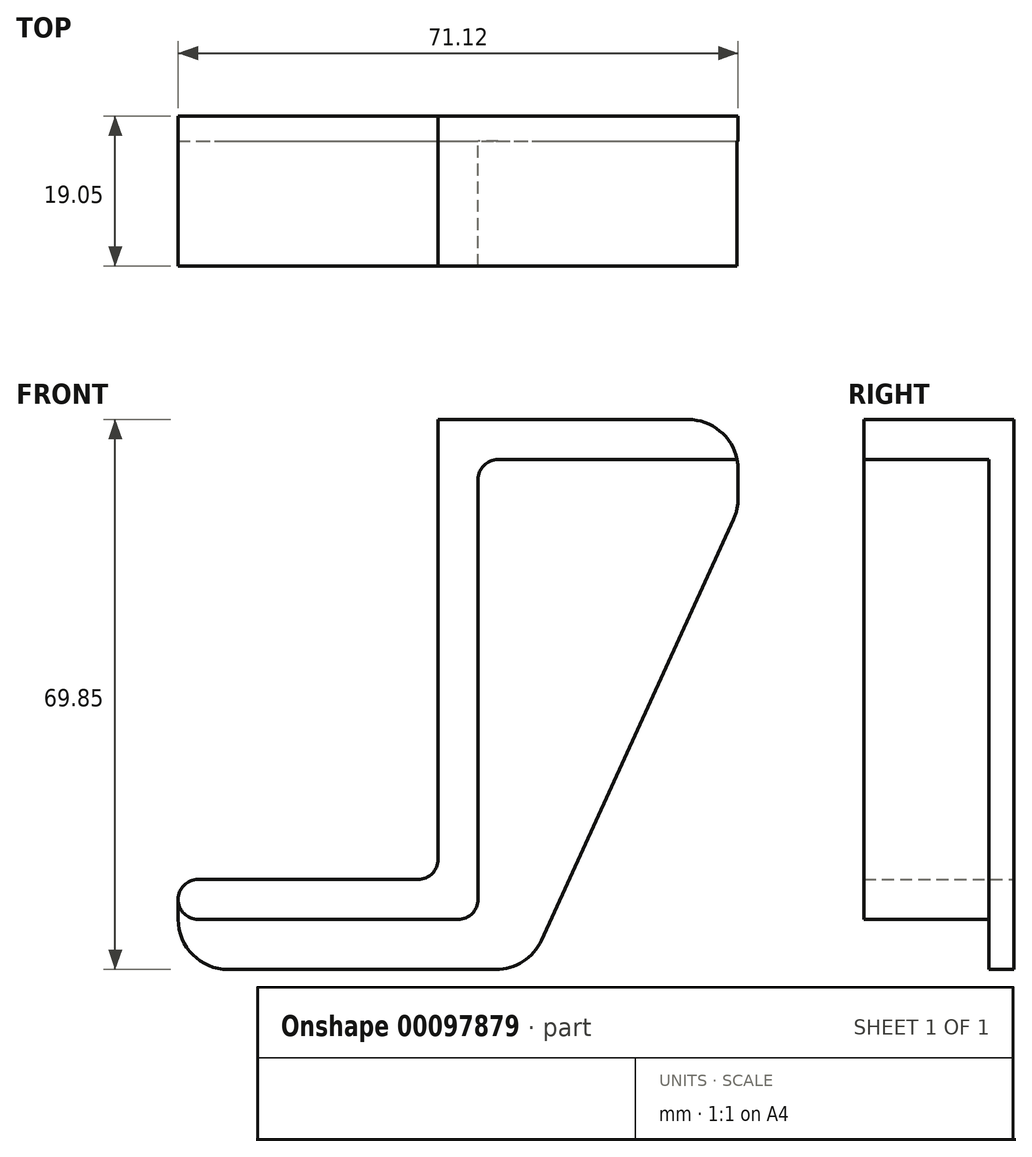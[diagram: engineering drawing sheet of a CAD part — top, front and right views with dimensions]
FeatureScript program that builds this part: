
annotation { "Feature Type Name" : "Feature", "Feature Type Description" : "" }
export const myFeature = defineFeature(function(context is Context, id is Id, definition is map)
    precondition{}
    {
        {
            var Q0;
            Q0=qCreatedBy(makeId("Front.planeOp"),FACE);
            var sketch = newSketch(context, id + "F0", { "sketchPlane" : qUnion([Q0])});
            skLineSegment(sketch, "E0.bottom", {"start": v(0, 0) * mm, "end": v(5.08, 0) * mm});
            skLineSegment(sketch, "E0.top", {"start": v(0, 63.5) * mm, "end": v(5.08, 63.5) * mm});
            skLineSegment(sketch, "E0.left", {"start": v(0, 5.08) * mm, "end": v(0, 63.5) * mm});
            skLineSegment(sketch, "E0.right", {"start": v(5.08, 0) * mm, "end": v(5.08, 58.42) * mm});
            skLineSegment(sketch, "E1.bottom", {"start": v(5.08, 0) * mm, "end": v(-33.02, 0) * mm});
            skLineSegment(sketch, "E1.top", {"start": v(0, 5.08) * mm, "end": v(-33.02, 5.08) * mm});
            skLineSegment(sketch, "E1.left", {"start": v(5.08, 0) * mm, "end": v(5.08, 5.08) * mm});
            skLineSegment(sketch, "E1.right", {"start": v(-33.02, 0) * mm, "end": v(-33.02, 5.08) * mm});
            skLineSegment(sketch, "E2.bottom", {"start": v(0, 63.5) * mm, "end": v(38.1, 63.5) * mm});
            skLineSegment(sketch, "E2.top", {"start": v(5.08, 58.42) * mm, "end": v(38.1, 58.42) * mm});
            skLineSegment(sketch, "E2.left", {"start": v(0, 63.5) * mm, "end": v(0, 58.42) * mm});
            skLineSegment(sketch, "E2.right", {"start": v(38.1, 63.5) * mm, "end": v(38.1, 58.42) * mm});
            skLineSegment(sketch, "E3.bottom", {"start": v(-33.02, 0) * mm, "end": v(5.08, 0) * mm});
            skLineSegment(sketch, "E3.top", {"start": v(-26.67, -6.35) * mm, "end": v(7.35, -6.35) * mm});
            skLineSegment(sketch, "E3.left", {"start": v(-33.02, 0) * mm, "end": v(-33.02, 0) * mm});
            skPoint(sketch, "E4.visualSharp", {"position": v(-33.02, -6.35) * mm});
            skArc(sketch, "E4.filletArc", {"start": v(-33.02, 0) * mm, "mid": v(-31.16, -4.5) * mm, "end": v(-26.67, -6.35) * mm});
            skLineSegment(sketch, "E5.bottom", {"start": v(38.1, 58.42) * mm, "end": v(5.08, 58.42) * mm});
            skLineSegment(sketch, "E5.left", {"start": v(38.1, 58.42) * mm, "end": v(38.1, 53.45) * mm});
            skLineSegment(sketch, "E6", {"start": v(13.13, -2.64) * mm, "end": v(37.53, 50.81) * mm});
            skPoint(sketch, "E7.visualSharp", {"position": v(38.1, 52.07) * mm});
            skArc(sketch, "E7.filletArc", {"start": v(37.53, 50.81) * mm, "mid": v(37.95, 52.1) * mm, "end": v(38.1, 53.45) * mm});
            skPoint(sketch, "E8.visualSharp", {"position": v(11.43, -6.35) * mm});
            skArc(sketch, "E8.filletArc", {"start": v(7.35, -6.35) * mm, "mid": v(10.78, -5.34) * mm, "end": v(13.13, -2.64) * mm});
            skSolve(sketch);
        }
        {
            var Q0;
            Q0=makeQuery(id+"F0.imprint","IMPRINT",FACE,{"disambiguationData":[TD([[makeQuery(id+"F0.imprint","IMPRINT",EDGE,{"derivedFrom":sQuery(id+"F0.wireOp",EDGE,"E0.left")}),-1.0]])]});
            extrude(context, id + "F1", {"entities" : qUnion([Q0]), "depth" : 19.05 * mm});
        }
        {
            var Q0;
            Q0=makeQuery(id+"F0.imprint","IMPRINT",FACE,{"disambiguationData":[TD([[makeQuery(id+"F0.imprint","IMPRINT",EDGE,{"derivedFrom":sQuery(id+"F0.wireOp",EDGE,"E0.right")}),-1.0]])]});
            extrude(context, id + "F2", {"entities" : qUnion([Q0]), "operationType" : NewBodyOperationType.ADD, "depth" : 3.17 * mm});
        }
        {
            var Q0;
            Q0=makeQuery(id+"F1.opExtrude","SWEPT_EDGE",EDGE,{"disambiguationData":[OSD([sQuery(id+"F0.wireOp",EDGE,"E2.bottom"),sQuery(id+"F0.wireOp",EDGE,"E2.left")])]});
            var Q1;
            Q1=makeQuery(id+"F1.opExtrude","SWEPT_EDGE",EDGE,{"disambiguationData":[OSD([sQuery(id+"F0.wireOp",EDGE,"E1.left"),sQuery(id+"F0.wireOp",EDGE,"E3.bottom")])]});
            fillet(context, id + "F3", {"entities" : qUnion([Q0, Q1]), "radius" : 6.35 * mm, "tangentPropagation" : true, "allowEdgeOverflow" : false});
        }
        {
            var Q0;
            Q0=makeQuery(id+"F2.boolean.opBoolean","SPLIT",EDGE,{"derivedFrom":makeQuery(id+"F1.opExtrude","SWEPT_EDGE",EDGE,{"disambiguationData":[OSD([sQuery(id+"F0.wireOp",EDGE,"E1.right"),sQuery(id+"F0.wireOp",EDGE,"E3.bottom"),sQuery(id+"F0.wireOp",EDGE,"E4.filletArc")])]})});
            var Q1;
            Q1=makeQuery(id+"F1.opExtrude","SWEPT_EDGE",EDGE,{"disambiguationData":[OSD([sQuery(id+"F0.wireOp",EDGE,"E1.top"),sQuery(id+"F0.wireOp",EDGE,"E1.right")])]});
            var Q2;
            Q2=makeQuery(id+"F1.opExtrude","SWEPT_EDGE",EDGE,{"disambiguationData":[OSD([sQuery(id+"F0.wireOp",EDGE,"E2.right"),sQuery(id+"F0.wireOp",EDGE,"E5.bottom"),sQuery(id+"F0.wireOp",EDGE,"E5.left")])]});
            var Q3;
            Q3=makeQuery(id+"F1.opExtrude","SWEPT_EDGE",EDGE,{"disambiguationData":[OSD([sQuery(id+"F0.wireOp",EDGE,"E2.bottom"),sQuery(id+"F0.wireOp",EDGE,"E2.right")])]});
            fillet(context, id + "F4", {"entities" : qUnion([Q0, Q1, Q2, Q3]), "radius" : 2.54 * mm, "tangentPropagation" : true, "allowEdgeOverflow" : false});
        }
        {
            var Q0;
            Q0=makeQuery(id+"F1.opExtrude","SWEPT_EDGE",EDGE,{"disambiguationData":[OSD([sQuery(id+"F0.wireOp",EDGE,"E0.right"),sQuery(id+"F0.wireOp",EDGE,"E5.bottom")])]});
            var Q1;
            Q1=makeQuery(id+"F1.opExtrude","SWEPT_EDGE",EDGE,{"disambiguationData":[OSD([sQuery(id+"F0.wireOp",EDGE,"E0.left"),sQuery(id+"F0.wireOp",EDGE,"E1.top")])]});
            fillet(context, id + "F5", {"entities" : qUnion([Q0, Q1]), "radius" : 2.54 * mm, "tangentPropagation" : true, "allowEdgeOverflow" : false});
        }
    });
